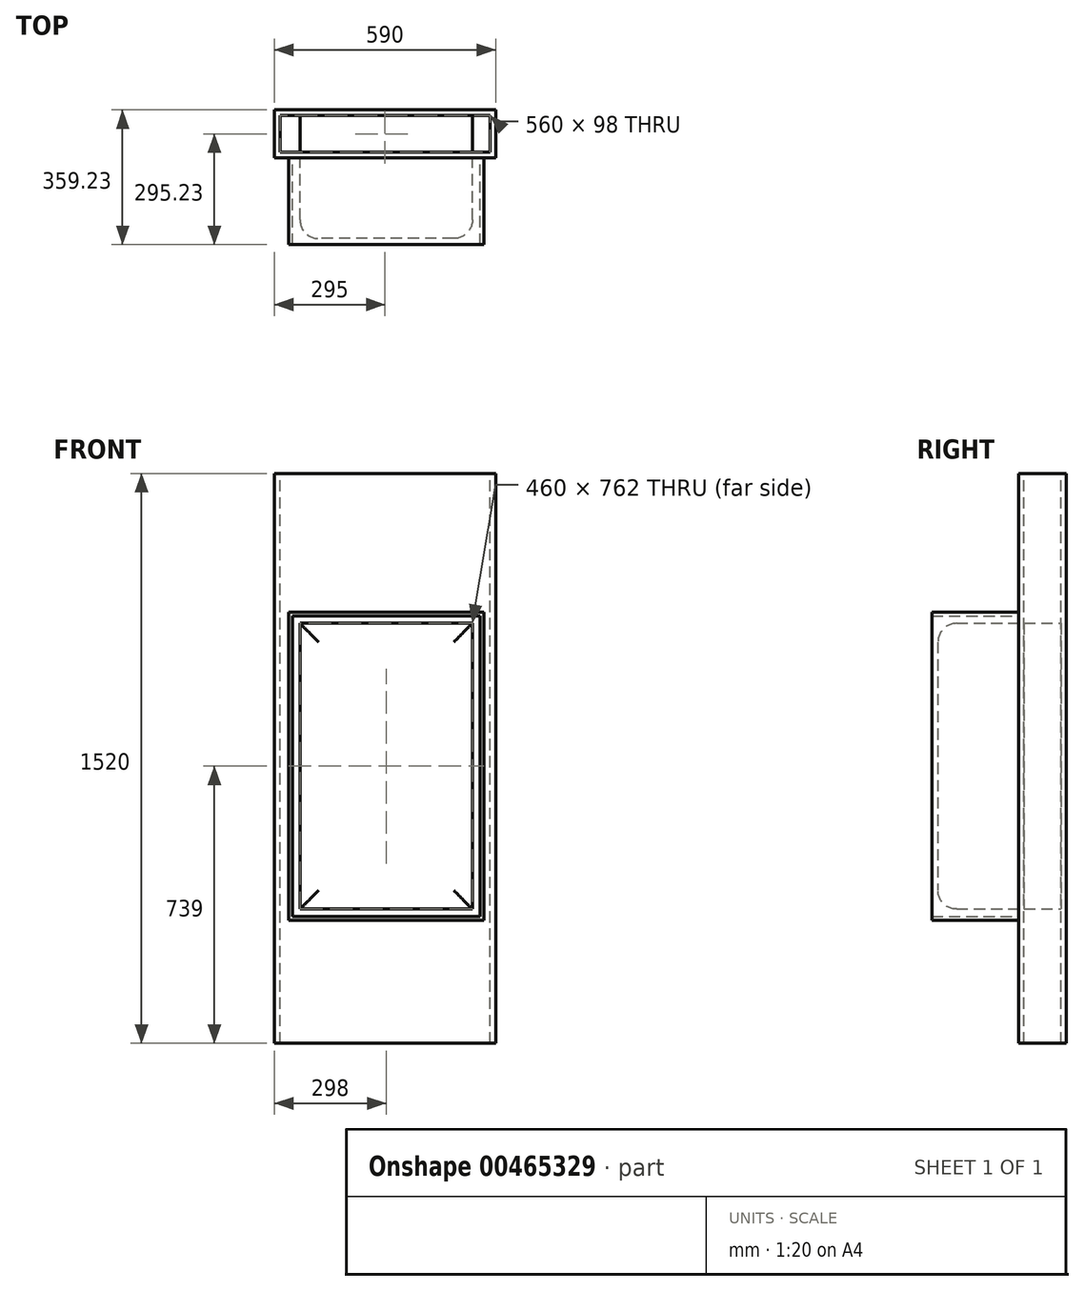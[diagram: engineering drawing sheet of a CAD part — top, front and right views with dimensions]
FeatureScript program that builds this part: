
annotation { "Feature Type Name" : "Feature", "Feature Type Description" : "" }
export const myFeature = defineFeature(function(context is Context, id is Id, definition is map)
    precondition{}
    {
        {
            var Q0;
            Q0=qCreatedBy(makeId("Top.planeOp"),FACE);
            var sketch = newSketch(context, id + "F0", { "sketchPlane" : qUnion([Q0])});
            skLineSegment(sketch, "E0.bottom", {"start": v(295, 64) * mm, "end": v(-295, 64) * mm});
            skLineSegment(sketch, "E0.top", {"start": v(295, -64) * mm, "end": v(-295, -64) * mm});
            skLineSegment(sketch, "E0.left", {"start": v(295, 64) * mm, "end": v(295, -64) * mm});
            skLineSegment(sketch, "E0.right", {"start": v(-295, 64) * mm, "end": v(-295, -64) * mm});
            skPoint(sketch, "E0.middle", {"position": v(0, 0) * mm});
            skSolve(sketch);
        }
        {
            var Q0;
            Q0 = qSketchRegion(id + "F0", true);
            extrude(context, id + "F1", {"entities" : qUnion([Q0]), "depth" : (358 + 762 + 400) * mm});
        }
        {
            var Q0;
            Q0=makeQuery(id+"F1.opExtrude","CAP_FACE",FACE,{"disambiguationData":[OSD([sQuery(id+"F0.wireOp",EDGE,"E0.bottom"),sQuery(id+"F0.wireOp",EDGE,"E0.top"),sQuery(id+"F0.wireOp",EDGE,"E0.left"),sQuery(id+"F0.wireOp",EDGE,"E0.right")])],"isStart":false});
            var sketch = newSketch(context, id + "F2", { "sketchPlane" : qUnion([Q0])});
            skLineSegment(sketch, "E1.0", {"start": v(295, 64) * mm, "end": v(-295, 64) * mm});
            skLineSegment(sketch, "E2.0", {"start": v(295, 64) * mm, "end": v(295, -64) * mm});
            skLineSegment(sketch, "E3.0", {"start": v(295, -64) * mm, "end": v(-295, -64) * mm});
            skLineSegment(sketch, "E4.0", {"start": v(-295, 64) * mm, "end": v(-295, -64) * mm});
            skLineSegment(sketch, "E5.0", {"start": v(280, 49) * mm, "end": v(-280, 49) * mm});
            skLineSegment(sketch, "E5.1", {"start": v(280, 49) * mm, "end": v(280, -49) * mm});
            skLineSegment(sketch, "E5.2", {"start": v(280, -49) * mm, "end": v(-280, -49) * mm});
            skLineSegment(sketch, "E5.3", {"start": v(-280, 49) * mm, "end": v(-280, -49) * mm});
            skSolve(sketch);
        }
        {
            var Q0;
            Q0=makeQuery(id+"F2.imprint","IMPRINT",FACE,{"disambiguationData":[TD([[makeQuery(id+"F2.imprint","IMPRINT",EDGE,{"derivedFrom":sQuery(id+"F2.wireOp",EDGE,"E5.0")}),1.0]])]});
            extrude(context, id + "F3", {"entities" : qUnion([Q0]), "operationType" : NewBodyOperationType.REMOVE, "endBound" : BoundingType.THROUGH_ALL, "oppositeDirection" : true, "depth" : 25 * mm});
        }
        {
            var Q0;
            Q0=makeQuery(id+"F1.opExtrude","SWEPT_FACE",FACE,{"disambiguationData":[OSD([sQuery(id+"F0.wireOp",EDGE,"E0.top")])]});
            var sketch = newSketch(context, id + "F4", { "sketchPlane" : qUnion([Q0])});
            skLineSegment(sketch, "E6", {"start": v(0, 1520) * mm, "end": v(0, 0) * mm, "construction": true});
            skLineSegment(sketch, "E7.bottom", {"start": v(233, 1120) * mm, "end": v(-227, 1120) * mm});
            skLineSegment(sketch, "E7.top", {"start": v(233, 358) * mm, "end": v(-227, 358) * mm});
            skLineSegment(sketch, "E7.left", {"start": v(233, 1120) * mm, "end": v(233, 358) * mm});
            skLineSegment(sketch, "E7.right", {"start": v(-227, 1120) * mm, "end": v(-227, 358) * mm});
            skPoint(sketch, "E7.middle", {"position": v(0, 760) * mm});
            skSolve(sketch);
        }
        {
            var Q0;
            Q0 = qSketchRegion(id + "F4", true);
            extrude(context, id + "F5", {"entities" : qUnion([Q0]), "operationType" : NewBodyOperationType.ADD, "depth" : 215 * mm, "hasSecondDirection" : true, "secondDirectionOppositeDirection" : true, "secondDirectionDepth" : 128 * mm});
        }
        {
            var Q0;
            Q0=makeQuery(id+"F5.opExtrude","CAP_EDGE",EDGE,{"disambiguationData":[OSD([sQuery(id+"F4.wireOp",EDGE,"E7.left")])],"isStart":false});
            var Q1;
            Q1=makeQuery(id+"F5.opExtrude","CAP_EDGE",EDGE,{"disambiguationData":[OSD([sQuery(id+"F4.wireOp",EDGE,"E7.right")])],"isStart":false});
            var Q2;
            Q2=makeQuery(id+"F5.opExtrude","CAP_EDGE",EDGE,{"disambiguationData":[OSD([sQuery(id+"F4.wireOp",EDGE,"E7.top")])],"isStart":false});
            var Q3;
            Q3=makeQuery(id+"F5.opExtrude","CAP_EDGE",EDGE,{"disambiguationData":[OSD([sQuery(id+"F4.wireOp",EDGE,"E7.bottom")])],"isStart":false});
            fillet(context, id + "F6", {"entities" : qUnion([Q0, Q1, Q2, Q3]), "radius" : 50 * mm, "tangentPropagation" : true, "allowEdgeOverflow" : false});
        }
        {
            var Q0;
            Q0=makeQuery(id+"F1.opExtrude","SWEPT_FACE",FACE,{"disambiguationData":[OSD([sQuery(id+"F0.wireOp",EDGE,"E0.top")])]});
            var sketch = newSketch(context, id + "F7", { "sketchPlane" : qUnion([Q0])});
            skLineSegment(sketch, "E8.bottom", {"start": v(-247, 1140) * mm, "end": v(253, 1140) * mm});
            skLineSegment(sketch, "E8.top", {"start": v(-247, 338) * mm, "end": v(253, 338) * mm});
            skLineSegment(sketch, "E8.left", {"start": v(-247, 1140) * mm, "end": v(-247, 338) * mm});
            skLineSegment(sketch, "E8.right", {"start": v(253, 1140) * mm, "end": v(253, 338) * mm});
            skLineSegment(sketch, "E9.0", {"start": v(-257, 328) * mm, "end": v(263, 328) * mm});
            skLineSegment(sketch, "E9.1", {"start": v(-257, 1150) * mm, "end": v(-257, 328) * mm});
            skLineSegment(sketch, "E9.2", {"start": v(-257, 1150) * mm, "end": v(263, 1150) * mm});
            skLineSegment(sketch, "E9.3", {"start": v(263, 1150) * mm, "end": v(263, 328) * mm});
            skSolve(sketch);
        }
        {
            var Q0;
            Q0 = qSketchRegion(id + "F7", true);
            extrude(context, id + "F8", {"entities" : qUnion([Q0]), "operationType" : NewBodyOperationType.ADD, "depth" : 231.23 * mm});
        }
    });
